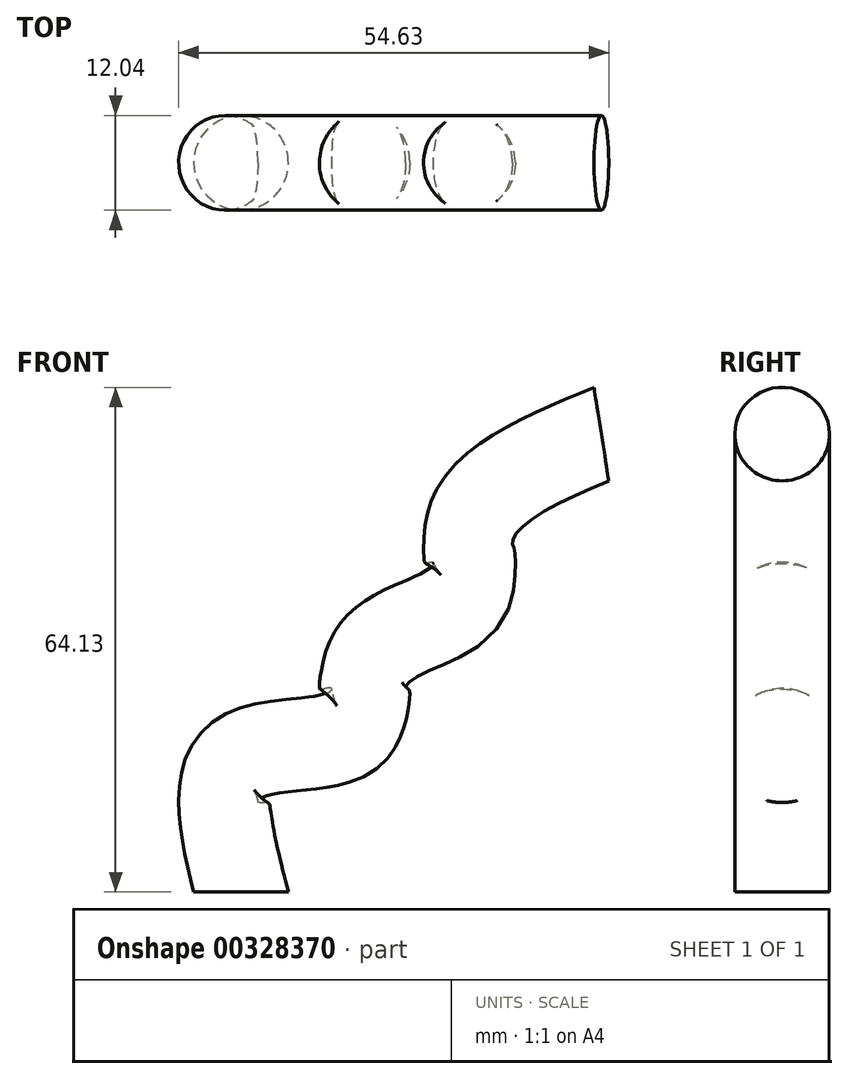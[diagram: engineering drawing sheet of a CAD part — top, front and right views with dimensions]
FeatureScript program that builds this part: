
annotation { "Feature Type Name" : "Feature", "Feature Type Description" : "" }
export const myFeature = defineFeature(function(context is Context, id is Id, definition is map)
    precondition{}
    {
        {
            var Q0;
            Q0=qCreatedBy(makeId("Front.planeOp"),FACE);
            var sketch = newSketch(context, id + "F0", { "sketchPlane" : qUnion([Q0])});
            skFitSpline(sketch, "E0", {"points": [v(0, 0) * mm, v(0, 16.88) * mm, v(13.77, 20.56) * mm, v(17.26, 30.45) * mm, v(27.93, 37.24) * mm, v(29.68, 47.52) * mm, v(45.78, 58.19) * mm], "startDerivative": vector(-28.61, 115.57) * mm, "endDerivative": vector(108.56, 45.88) * mm});
            skSolve(sketch);
        }
        {
            var Q0;
            Q0=qCreatedBy(makeId("Top.planeOp"),FACE);
            var sketch = newSketch(context, id + "F1", { "sketchPlane" : qUnion([Q0])});
            skCircle(sketch, "E1", {"center": v(0, 0) * mm, "radius": 6.02 * mm});
            skSolve(sketch);
        }
        {
            var Q0;
            Q0=makeQuery(id+"F1.imprint","IMPRINT",FACE,{"disambiguationData":[TD([[makeQuery(id+"F1.imprint","IMPRINT",EDGE,{"derivedFrom":sQuery(id+"F1.wireOp",EDGE,"E1")}),1.0]])]});
            var Q1;
            Q1=sQuery(id+"F0.wireOp",EDGE,"E0");
            sweep(context, id + "F2", {"profiles" : qUnion([Q0]), "path" : qUnion([Q1])});
        }
    });
